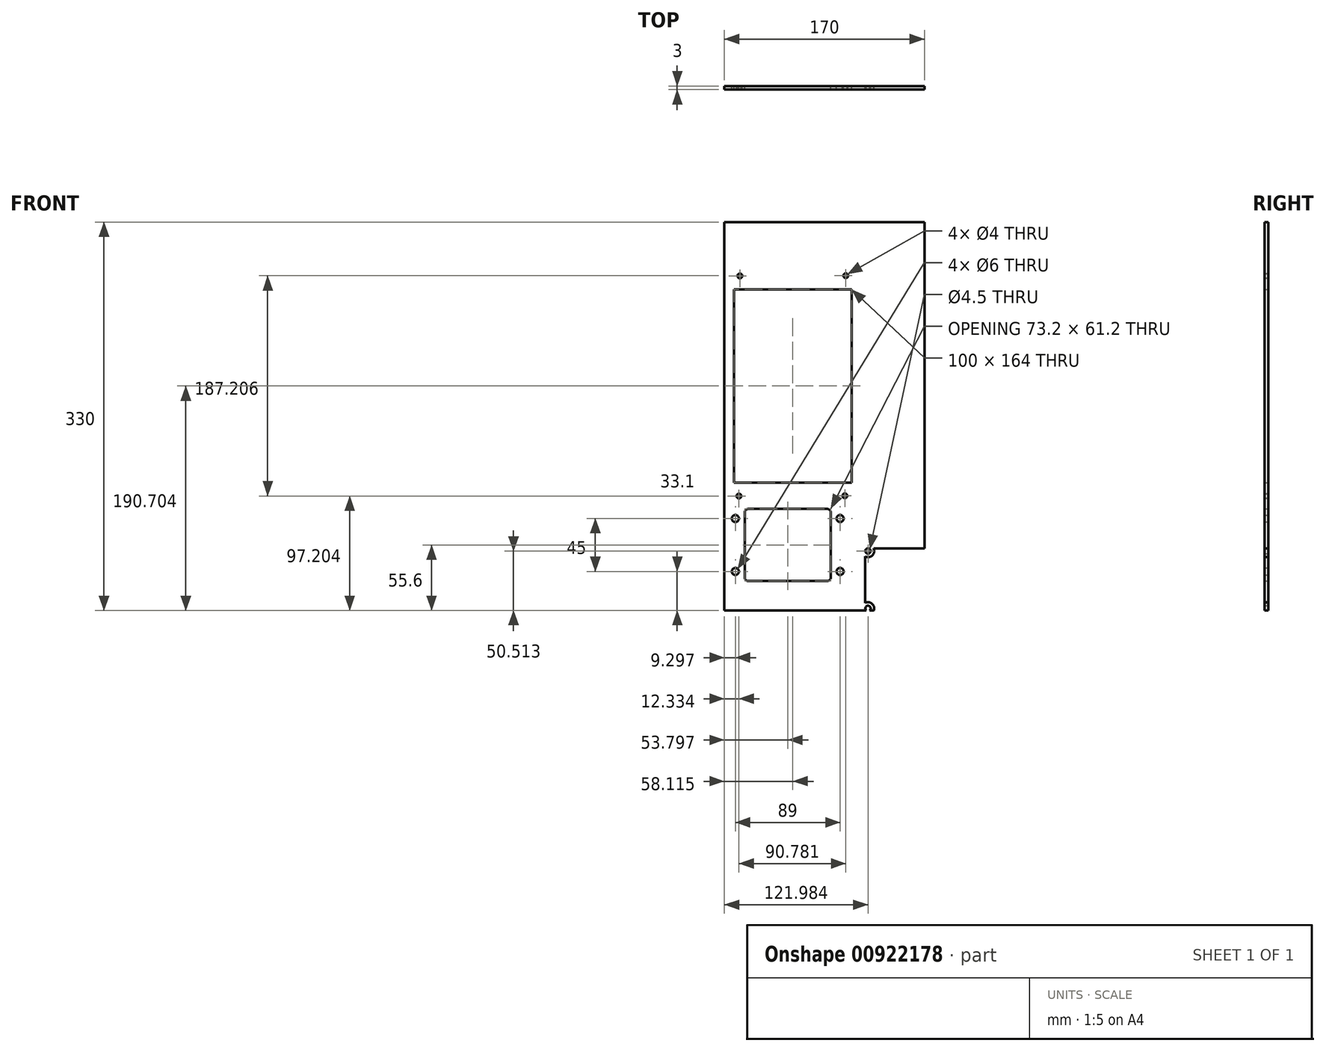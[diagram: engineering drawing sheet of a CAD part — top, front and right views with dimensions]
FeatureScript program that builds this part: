
annotation { "Feature Type Name" : "Feature", "Feature Type Description" : "" }
export const myFeature = defineFeature(function(context is Context, id is Id, definition is map)
    precondition{}
    {
        {
            var Q0;
            Q0=qCreatedBy(makeId("Front.planeOp"),FACE);
            var sketch = newSketch(context, id + "F0", { "sketchPlane" : qUnion([Q0])});
            skCircle(sketch, "E0", {"center": v(-21.22, 58.52) * mm, "radius": 3 * mm});
            skLineSegment(sketch, "E1.bottom", {"start": v(-10.32, 66.62) * mm, "end": v(56.88, 66.62) * mm});
            skLineSegment(sketch, "E1.top", {"start": v(-10.32, 5.42) * mm, "end": v(56.88, 5.42) * mm});
            skLineSegment(sketch, "E1.left", {"start": v(-13.32, 63.62) * mm, "end": v(-13.32, 8.42) * mm});
            skLineSegment(sketch, "E1.right", {"start": v(59.88, 63.62) * mm, "end": v(59.88, 8.42) * mm});
            skPoint(sketch, "E2.visualSharp", {"position": v(-13.32, 66.62) * mm});
            skArc(sketch, "E2.filletArc", {"start": v(-10.32, 66.62) * mm, "mid": v(-12.44, 65.74) * mm, "end": v(-13.32, 63.62) * mm});
            skPoint(sketch, "E3.visualSharp", {"position": v(59.88, 66.62) * mm});
            skArc(sketch, "E3.filletArc", {"start": v(59.88, 63.62) * mm, "mid": v(59, 65.74) * mm, "end": v(56.88, 66.62) * mm});
            skPoint(sketch, "E4.visualSharp", {"position": v(59.88, 5.42) * mm});
            skArc(sketch, "E4.filletArc", {"start": v(56.88, 5.42) * mm, "mid": v(59, 6.3) * mm, "end": v(59.88, 8.42) * mm});
            skPoint(sketch, "E5.visualSharp", {"position": v(-13.32, 5.42) * mm});
            skArc(sketch, "E5.filletArc", {"start": v(-13.32, 8.42) * mm, "mid": v(-12.44, 6.3) * mm, "end": v(-10.32, 5.42) * mm});
            skCircle(sketch, "E6", {"center": v(67.78, 58.52) * mm, "radius": 3 * mm});
            skCircle(sketch, "E7", {"center": v(67.78, 13.52) * mm, "radius": 3 * mm});
            skCircle(sketch, "E8", {"center": v(-21.22, 13.52) * mm, "radius": 3 * mm});
            skLineSegment(sketch, "E9", {"start": v(23.28, 66.62) * mm, "end": v(23.28, 5.42) * mm});
            skLineSegment(sketch, "E10", {"start": v(-13.32, 36.02) * mm, "end": v(59.88, 36.02) * mm});
            skLineSegment(sketch, "E11.bottom", {"start": v(-22.4, 253.12) * mm, "end": v(77.6, 253.12) * mm});
            skLineSegment(sketch, "E11.top", {"start": v(-22.4, 89.12) * mm, "end": v(77.6, 89.12) * mm});
            skLineSegment(sketch, "E11.left", {"start": v(-22.4, 253.12) * mm, "end": v(-22.4, 89.12) * mm});
            skLineSegment(sketch, "E11.right", {"start": v(77.6, 253.12) * mm, "end": v(77.6, 89.12) * mm});
            skLineSegment(sketch, "E12.top", {"start": v(96.08, -20.32) * mm, "end": v(155.6, -20.32) * mm});
            skLineSegment(sketch, "E12.left", {"start": v(88.96, 26.32) * mm, "end": v(88.96, -13.2) * mm});
            skLineSegment(sketch, "E12.right", {"start": v(162.46, 26.07) * mm, "end": v(162.46, -20.32) * mm});
            skCircle(sketch, "E13", {"center": v(91.46, 30.93) * mm, "radius": 2.25 * mm});
            skCircle(sketch, "E14", {"center": v(159.96, 30.68) * mm, "radius": 2.25 * mm});
            skCircle(sketch, "E15", {"center": v(91.46, -17.82) * mm, "radius": 2.25 * mm});
            skCircle(sketch, "E16", {"center": v(160.21, -17.82) * mm, "radius": 2.25 * mm});
            skArc(sketch, "E17", {"start": v(96.08, -20.32) * mm, "mid": v(95.18, -14.1) * mm, "end": v(88.96, -13.2) * mm});
            skArc(sketch, "E18", {"start": v(88.96, 26.32) * mm, "mid": v(95.08, 27.12) * mm, "end": v(96.2, 33.18) * mm});
            skArc(sketch, "E19", {"start": v(155.35, 33.18) * mm, "mid": v(156.25, 26.97) * mm, "end": v(162.46, 26.07) * mm});
            skArc(sketch, "E20", {"start": v(162.46, -13.07) * mm, "mid": v(156.4, -14.2) * mm, "end": v(155.6, -20.32) * mm});
            skLineSegment(sketch, "E21.trimOffspring", {"start": v(96.2, 33.18) * mm, "end": v(155.35, 33.18) * mm});
            skCircle(sketch, "E22", {"center": v(-17.4, 264.62) * mm, "radius": 2 * mm});
            skCircle(sketch, "E23", {"center": v(72.6, 264.83) * mm, "radius": 2 * mm});
            skCircle(sketch, "E24", {"center": v(-18.19, 77.62) * mm, "radius": 2 * mm});
            skCircle(sketch, "E25", {"center": v(71.81, 77.83) * mm, "radius": 2 * mm});
            skLineSegment(sketch, "E26.bottom", {"start": v(-30.52, 310.42) * mm, "end": v(139.48, 310.42) * mm});
            skLineSegment(sketch, "E26.top", {"start": v(-30.52, -19.58) * mm, "end": v(139.48, -19.58) * mm});
            skLineSegment(sketch, "E26.left", {"start": v(139.48, 310.42) * mm, "end": v(139.48, -19.58) * mm});
            skLineSegment(sketch, "E26.right", {"start": v(-30.52, 310.42) * mm, "end": v(-30.52, -19.58) * mm});
            skSolve(sketch);
        }
        {
            var Q0;
            Q0=makeQuery(id+"F0.imprint","IMPRINT",FACE,{"disambiguationData":[TD([[makeQuery(id+"F0.imprint","IMPRINT",EDGE,{"derivedFrom":sQuery(id+"F0.wireOp",EDGE,"E0")}),-1.0]])]});
            extrude(context, id + "F1", {"entities" : qUnion([Q0]), "depth" : 3 * mm, "offsetDistance" : 25 * mm});
        }
    });
